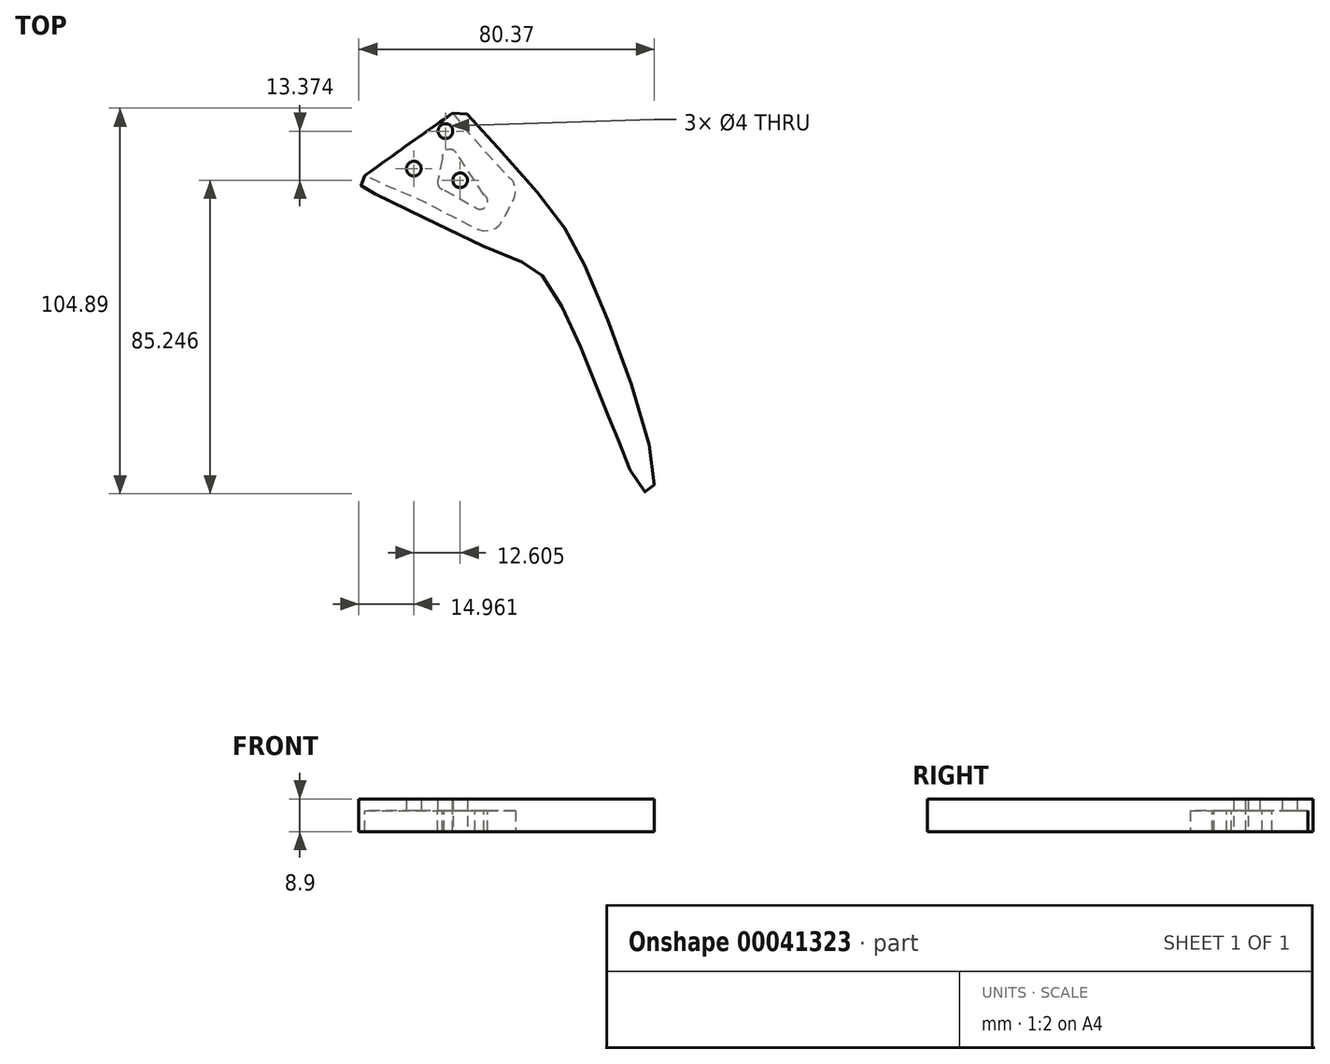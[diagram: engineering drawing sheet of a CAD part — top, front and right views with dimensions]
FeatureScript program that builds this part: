
annotation { "Feature Type Name" : "Feature", "Feature Type Description" : "" }
export const myFeature = defineFeature(function(context is Context, id is Id, definition is map)
    precondition{}
    {
        {
            var Q0;
            Q0=qCreatedBy(makeId("Top.planeOp"),FACE);
            var sketch = newSketch(context, id + "F0", { "sketchPlane" : qUnion([Q0])});
            skCircle(sketch, "E0", {"center": v(10.1, 5.55) * mm, "radius": 1.59 * mm});
            skFitSpline(sketch, "E1", {"points": [v(22.87, -11.33) * mm, v(22.87, -12.3) * mm, v(22.45, -13.63) * mm, v(20.7, -15.8) * mm, v(19.17, -16) * mm, v(9.26, -10.98) * mm, v(8.43, -10.42) * mm, v(7.87, -9.65) * mm, v(7.59, -8.75) * mm, v(7.73, -6.93) * mm, v(8.5, -2.4) * mm, v(8.84, -0.8) * mm, v(9.75, 0.67) * mm, v(10.8, 1.02) * mm, v(11.84, 1.02) * mm, v(12.82, 0.6) * mm, v(14.7, -1.21) * mm, v(16.17, -3.1) * mm, v(22.87, -11.33) * mm]});
            skFitSpline(sketch, "E2", {"points": [v(7.52, 11.7) * mm, v(8.29, 11.76) * mm, v(9.47, 11.9) * mm, v(11, 12.04) * mm, v(11.29, 11.55) * mm, v(27.6, -7.28) * mm, v(28.52, -8.19) * mm, v(28.86, -9.3) * mm, v(29.14, -10.63) * mm, v(28.93, -12.1) * mm, v(28.3, -13.7) * mm, v(24.96, -19.84) * mm, v(24.4, -20.6) * mm, v(23.35, -21.16) * mm, v(21.75, -21.58) * mm, v(19.87, -21.58) * mm, v(18.47, -21.02) * mm, v(15.96, -19.77) * mm, v(12.54, -17.96) * mm, v(8.15, -15.72) * mm, v(2.78, -13) * mm, v(-14.25, -5) * mm, v(-14.8, -3.72) * mm, v(-14.8, -2.75) * mm, v(-12.92, 0) * mm, v(-11.73, 0.74) * mm, v(4.24, 11.41) * mm, v(4.59, 11.55) * mm, v(7.52, 11.7) * mm]});
            skCircle(sketch, "E3", {"center": v(10.1, 5.55) * mm, "radius": 0.94 * mm});
            skCircle(sketch, "E4", {"center": v(19.54, -13.61) * mm, "radius": 2.1 * mm});
            skCircle(sketch, "E5", {"center": v(11.34, -1.54) * mm, "radius": 2.1 * mm});
            skFitSpline(sketch, "E6", {"points": [v(-13.41, -8) * mm, v(-13.06, -7.47) * mm, v(13.76, 11.55) * mm, v(14.64, 11.55) * mm, v(35.47, -11.53) * mm, v(49.26, -33.85) * mm, v(66.35, -83.97) * mm, v(65.82, -93.06) * mm, v(62.17, -90.05) * mm, v(57.02, -78.07) * mm, v(53.45, -69.75) * mm, v(45.17, -49.3) * mm, v(35.47, -32.7) * mm, v(25.58, -27.94) * mm, v(-11.3, -10.47) * mm, v(-12.53, -9.77) * mm, v(-13.41, -8) * mm]});
            skCircle(sketch, "E7", {"center": v(10.07, -8.4) * mm, "radius": 2.1 * mm});
            skLineSegment(sketch, "E8", {"start": v(9.79, -10.47) * mm, "end": v(18.1, -15.14) * mm});
            skLineSegment(sketch, "E9", {"start": v(18.1, -15.14) * mm, "end": v(20.56, -11.78) * mm});
            skLineSegment(sketch, "E10", {"start": v(20.56, -11.78) * mm, "end": v(13.1, -0.39) * mm});
            skLineSegment(sketch, "E11", {"start": v(13.1, -0.39) * mm, "end": v(9.31, -2.06) * mm});
            skLineSegment(sketch, "E12", {"start": v(9.31, -2.06) * mm, "end": v(8.02, -7.95) * mm});
            skLineSegment(sketch, "E13", {"start": v(8.02, -7.95) * mm, "end": v(9.79, -10.47) * mm});
            skSolve(sketch);
        }
        {
            var Q0;
            {var subQ0=sQuery(id+"F0.wireOp",EDGE,"E6");var subQ1=sQuery(id+"F0.wireOp",EDGE,"E2");var subQ3=makeQuery(id+"F0.imprint","INTERSECT",VERTEX,{"disambiguationData":[OD(0.0)],"derivedFrom":[subQ1,subQ0]});Q0=makeQuery(id+"F0.imprint","IMPRINT",FACE,{"disambiguationData":[TD([[makeQuery(id+"F0.imprint","IMPRINT",EDGE,{"disambiguationData":[TD([[subQ3,1.0]])],"derivedFrom":subQ1}),1.0]])]});}
            var Q1;
            Q1=makeQuery(id+"F0.imprint","IMPRINT",FACE,{"disambiguationData":[TD([[makeQuery(id+"F0.imprint","IMPRINT",EDGE,{"derivedFrom":sQuery(id+"F0.wireOp",EDGE,"E0")}),-1.0]])]});
            var Q2;
            Q2=makeQuery(id+"F0.imprint","IMPRINT",FACE,{"disambiguationData":[TD([[makeQuery(id+"F0.imprint","IMPRINT",EDGE,{"derivedFrom":sQuery(id+"F0.wireOp",EDGE,"E1")}),-1.0]])]});
            var Q3;
            Q3=makeQuery(id+"F0.imprint","IMPRINT",FACE,{"disambiguationData":[TD([[makeQuery(id+"F0.imprint","IMPRINT",EDGE,{"derivedFrom":sQuery(id+"F0.wireOp",EDGE,"E5")}),1.0]])]});
            var Q4;
            Q4=makeQuery(id+"F0.imprint","IMPRINT",FACE,{"disambiguationData":[TD([[makeQuery(id+"F0.imprint","IMPRINT",EDGE,{"derivedFrom":sQuery(id+"F0.wireOp",EDGE,"E4")}),1.0]])]});
            var Q5;
            Q5=makeQuery(id+"F0.imprint","IMPRINT",FACE,{"disambiguationData":[TD([[makeQuery(id+"F0.imprint","IMPRINT",EDGE,{"derivedFrom":sQuery(id+"F0.wireOp",EDGE,"E0")}),1.0]])]});
            var Q6;
            Q6=makeQuery(id+"F0.imprint","IMPRINT",FACE,{"disambiguationData":[TD([[makeQuery(id+"F0.imprint","IMPRINT",EDGE,{"derivedFrom":sQuery(id+"F0.wireOp",EDGE,"E3")}),1.0]])]});
            var Q7;
            Q7=sQuery(id+"F0.wireOp",EDGE,"E6");
            extrude(context, id + "F1", {"entities" : qUnion([Q0, Q1, Q2, Q3, Q4, Q5, Q6]), "surfaceEntities" : qUnion([Q7]), "depth" : 3.17 * mm});
        }
        {
            var Q0;
            Q0=makeQuery(id+"F0.imprint","IMPRINT",FACE,{"disambiguationData":[TD([[makeQuery(id+"F0.imprint","IMPRINT",EDGE,{"derivedFrom":sQuery(id+"F0.wireOp",EDGE,"E3")}),1.0]])]});
            var Q1;
            Q1=makeQuery(id+"F0.imprint","IMPRINT",FACE,{"disambiguationData":[TD([[makeQuery(id+"F0.imprint","IMPRINT",EDGE,{"derivedFrom":sQuery(id+"F0.wireOp",EDGE,"E5")}),1.0]])]});
            var Q2;
            Q2=makeQuery(id+"F0.imprint","IMPRINT",FACE,{"disambiguationData":[TD([[makeQuery(id+"F0.imprint","IMPRINT",EDGE,{"derivedFrom":sQuery(id+"F0.wireOp",EDGE,"E4")}),1.0]])]});
            var Q3;
            {var subQ0=sQuery(id+"F0.wireOp",EDGE,"E8");Q3=makeQuery(id+"F0.imprint","IMPRINT",FACE,{"disambiguationData":[TD([[makeQuery(id+"F0.imprint","IMPRINT",EDGE,{"derivedFrom":subQ0}),1.0]])]});}
            var Q4;
            {var subQ0=sQuery(id+"F0.wireOp",EDGE,"E13");Q4=makeQuery(id+"F0.imprint","IMPRINT",FACE,{"disambiguationData":[TD([[makeQuery(id+"F0.imprint","IMPRINT",EDGE,{"derivedFrom":subQ0}),1.0]])]});}
            var Q5;
            {var subQ0=sQuery(id+"F0.wireOp",EDGE,"E13");Q5=makeQuery(id+"F0.imprint","IMPRINT",FACE,{"disambiguationData":[TD([[makeQuery(id+"F0.imprint","IMPRINT",EDGE,{"derivedFrom":subQ0}),-1.0]])]});}
            var Q6;
            Q6=sQuery(id+"F0.wireOp",EDGE,"E3");
            var Q7;
            Q7=sQuery(id+"F0.wireOp",EDGE,"E5");
            var Q8;
            Q8=sQuery(id+"F0.wireOp",EDGE,"E4");
            var Q9;
            Q9=makeQuery(id+"F1.opExtrude","CAP_FACE",FACE,{"disambiguationData":[OSD([sQuery(id+"F0.wireOp",EDGE,"E4"),sQuery(id+"F0.wireOp",EDGE,"E5"),sQuery(id+"F0.wireOp",EDGE,"E6"),sQuery(id+"F0.wireOp",EDGE,"E7"),sQuery(id+"F0.wireOp",EDGE,"E8"),sQuery(id+"F0.wireOp",EDGE,"E10"),sQuery(id+"F0.wireOp",EDGE,"E12")])],"isStart":false});
            extrude(context, id + "F2", {"entities" : qUnion([Q0, Q1, Q2, Q3, Q4, Q5]), "operationType" : NewBodyOperationType.ADD, "surfaceEntities" : qUnion([Q6, Q7, Q8]), "oppositeDirection" : true, "offsetDistance" : 25.4 * mm, "depth" : 5.7 * mm, "hasSecondDirection" : true, "secondDirectionBound" : SecondDirectionBoundingType.UP_TO_SURFACE, "secondDirectionOppositeDirection" : false, "secondDirectionBoundEntityFace" : qUnion([Q9]), "secondDirectionDepth" : 2.54 * mm});
        }
        {
            var Q0;
            {var subQ0=sQuery(id+"F0.wireOp",EDGE,"E6");var subQ1=sQuery(id+"F0.wireOp",EDGE,"E2");var subQ3=makeQuery(id+"F0.imprint","INTERSECT",VERTEX,{"disambiguationData":[OD(0.0)],"derivedFrom":[subQ1,subQ0]});Q0=makeQuery(id+"F0.imprint","IMPRINT",FACE,{"disambiguationData":[TD([[makeQuery(id+"F0.imprint","IMPRINT",EDGE,{"disambiguationData":[TD([[subQ3,1.0]])],"derivedFrom":subQ1}),1.0]])]});}
            extrude(context, id + "F3", {"entities" : qUnion([Q0]), "operationType" : NewBodyOperationType.ADD, "oppositeDirection" : true, "depth" : 5.7 * mm});
        }
        {
            var Q0;
            Q0=makeQuery(id+"F0.imprint","IMPRINT",FACE,{"disambiguationData":[TD([[makeQuery(id+"F0.imprint","IMPRINT",EDGE,{"derivedFrom":sQuery(id+"F0.wireOp",EDGE,"E0")}),-1.0]])]});
            var sketch = newSketch(context, id + "F4", { "sketchPlane" : qUnion([Q0])});
            skCircle(sketch, "E14", {"center": v(1.52, -4.68) * mm, "radius": 2 * mm});
            skSolve(sketch);
        }
        {
            var Q0;
            Q0 = qSketchRegion(id + "F4", true);
            extrude(context, id + "F5", {"entities" : qUnion([Q0]), "operationType" : NewBodyOperationType.REMOVE, "depth" : 25.4 * mm, "offsetDistance" : 25.4 * mm});
        }
        {
            var Q0;
            Q0=makeQuery(id+"F2.opExtrude","CAP_FACE",FACE,{"disambiguationData":[OSD([sQuery(id+"F0.wireOp",EDGE,"E4"),sQuery(id+"F0.wireOp",EDGE,"E5"),sQuery(id+"F0.wireOp",EDGE,"E7"),sQuery(id+"F0.wireOp",EDGE,"E8"),sQuery(id+"F0.wireOp",EDGE,"E10"),sQuery(id+"F0.wireOp",EDGE,"E12")])],"isStart":false});
            var sketch = newSketch(context, id + "F6", { "sketchPlane" : qUnion([Q0])});
            skCircle(sketch, "E15", {"center": v(14.13, 7.84) * mm, "radius": 2 * mm});
            skSolve(sketch);
        }
        {
            var Q0;
            Q0 = qSketchRegion(id + "F6", true);
            extrude(context, id + "F7", {"entities" : qUnion([Q0]), "operationType" : NewBodyOperationType.REMOVE, "oppositeDirection" : true, "depth" : 25.4 * mm, "offsetDistance" : 25.4 * mm});
        }
        {
            var Q0;
            Q0=makeQuery(id+"F0.imprint","IMPRINT",FACE,{"disambiguationData":[TD([[makeQuery(id+"F0.imprint","IMPRINT",EDGE,{"derivedFrom":sQuery(id+"F0.wireOp",EDGE,"E0")}),-1.0]])]});
            var sketch = newSketch(context, id + "F8", { "sketchPlane" : qUnion([Q0])});
            skCircle(sketch, "E16", {"center": v(10.1, 5.53) * mm, "radius": 2 * mm});
            skSolve(sketch);
        }
        {
            var Q0;
            Q0 = qSketchRegion(id + "F8", true);
            extrude(context, id + "F9", {"entities" : qUnion([Q0]), "operationType" : NewBodyOperationType.REMOVE, "oppositeDirection" : true, "depth" : 25.4 * mm, "offsetDistance" : 25.4 * mm, "hasSecondDirection" : true, "secondDirectionOppositeDirection" : false, "secondDirectionDepth" : 25.4 * mm});
        }
    });
